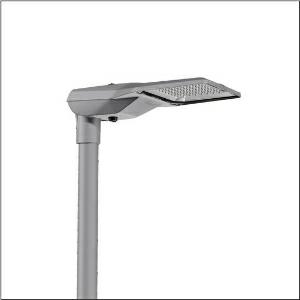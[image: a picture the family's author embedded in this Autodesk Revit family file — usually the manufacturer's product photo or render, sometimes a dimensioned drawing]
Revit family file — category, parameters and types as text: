
# Revit family: streetlight_sl_21_iq_midi___stw1_0a_5xe3e31y08mb_1dd4
name_source: partatom
category: Lighting Fixtures
units: mm (PartAtom-declared; Revit-internal decimal feet)

## family parameters
Cut with Voids When Loaded = No
Host = Face
Light Source = No
Part Type = Normal
Room Calculation Point = No
Round Connector Dimension = Use Diameter
Shared = No

## types (1)
- --- (1 x LED, 18340 lm, 129.3 W, 3000K)
    Apparent Load = 129 VA
    CIE Flux Codes = 38 75 98 100 100
    Color Rendering = 70
    Color Temperature = 3000K
    Default Elevation = 1800 mm
    Description = Streetlight SL 21 iQ midi, mast luminaire, primary light control with lens, of PMMA, primary optical cover: cover, of toughened safety glass, transparent, light distribution: STW1.0a, light emission: direct distribution, primary light characteristic: asymmetric, installation type: post-top, side-entry, LED, High Power LED, rated luminous flux: 18.340lm, luminous efficacy: 142lm/W, light colour: 730, colour temperature: 3000K, control gear: iQ-Street Remote, D4i with power reduction, control: pre-setting: logarithmic dimming characteristic, Street-Remote, Auto-Match, Temp-Guard, Lumen-Switch, Night-Set, Smart-Wire, Light-Fading, Desk-Remote (wireless, voltage-free reading and setting of iQ features in the workshop via application-optimized NFC function/RFID function), optimised constant luminous flux control (CLO 2.0), mains connection: 230..240V, AC, 50/60Hz, start of lifetime: 129W, end of service life: 142W, reduction: 56W, luminaire housing, of diecast aluminium, powder-coated, SITECO metallic grey (DB 702S), corrosivity category C5 high according to DIN EN ISO 12944, please order mast flange separately, inclination adjustable: 0°, 5°, 10°, 15°, sealing non-destructively replaceable, multi-level sealing system, length: 644mm, width: 335mm, height: 110mm, mast flange for spigot size: 42mm (side-entry): 5XC10008XM4, 60/48mm (side-entry/post-top): 5XC10108XM2, 76/60mm (side-entry/post-top): 5XC10108XM1, mounting height: 4..8m, Smart Interface below and above, protection rating (complete): IP66, insulation class (complete): insulation class II (safety insulation), certification: CE, ENEC, ENEC+, VDE, impact resistance: IK10, permissible operating ambient temperature for outdoor applications: -40..+50°C, standard-compliant lighting for roads and squares, packaging unit: 1 piece

Light Distribution: STW1.0a
    Height = 111 mm
    Lamp = 1 x LED
    Lamp Light Flux = 18340 lm
    Lamp Power = 129.3 W
    Lamp count = 1
    Length = 644 mm
    Luminous efficacy = 142 lm/W
    Manufacturer = Siteco
    ModVariant = No
    Model = 5XE3E31Y08MB
    Number of Poles = 1
    OnlyDefault = Yes
    Power Factor = 1
    Product Name = Streetlight SL 21 iQ midi | STW1.0a
    Product group = mast luminaire | pylon top
    ProductGroupID = 6100
    Protection Class = Protection class II
    Protection Degree = IP 66
    RLX_Detail_Level = 1
    RLX_Emergency_Light_Flux = 0 lm
    RLX_Emergency_Type = 0
    RLX_Emergency_Type_DB = No
    RlxData = <blob elided: 91289 chars, md5=aacf74b3>
    Socket = socket
    Standby Power = 0 W
    System Light Flux = 18340 lm
    System Power = 129 W
    Type Comments = factory setting: luminous flux: 100 % | dim-lin: 254 | 672 mA
    Type Image = l_1004304.jpg
    URL = http://relux.com
    VarID = @adj_114385
    Voltage = 0 V
    Weight = 0.00 kg
    Width = 336 mm

## geometry (parser evidence)
native form markers: Blend x4, Sweep x9
no freeform markers — native parametric forms only
